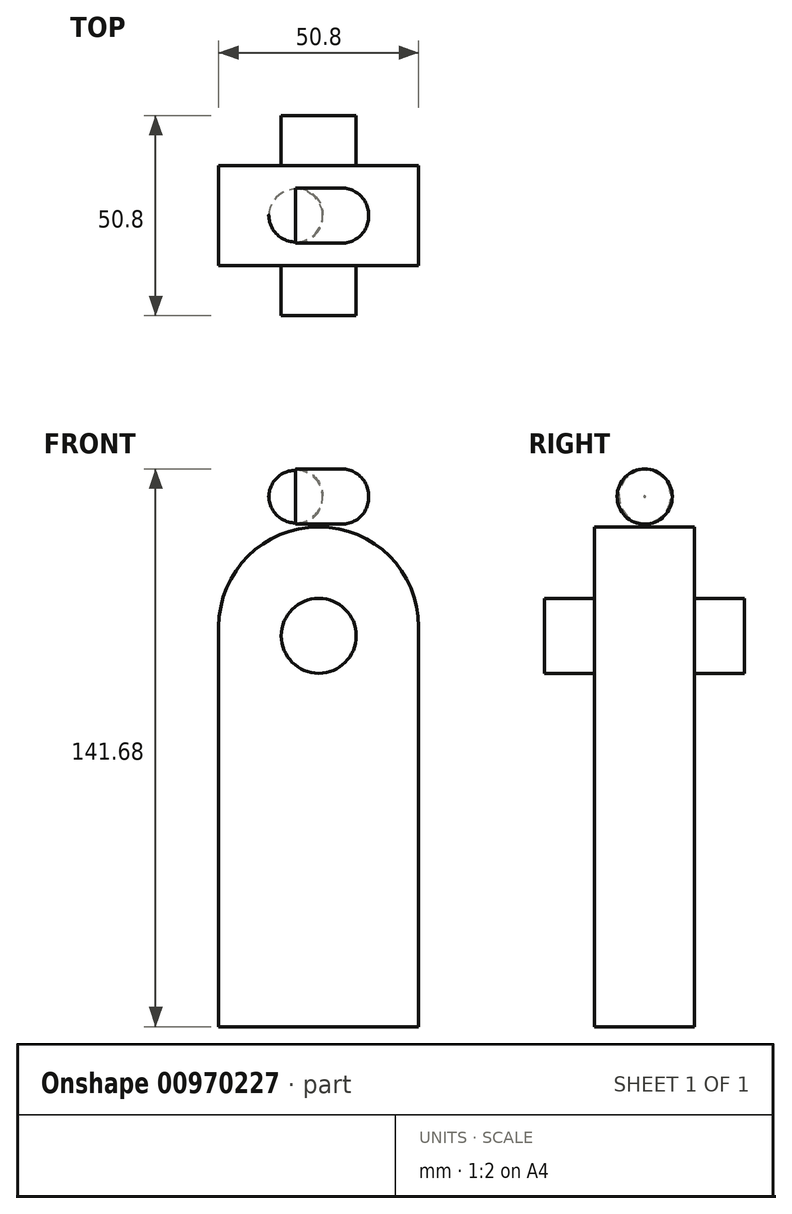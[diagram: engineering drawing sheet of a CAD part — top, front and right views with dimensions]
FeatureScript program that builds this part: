
annotation { "Feature Type Name" : "Feature", "Feature Type Description" : "" }
export const myFeature = defineFeature(function(context is Context, id is Id, definition is map)
    precondition{}
    {
        {
            var Q0;
            Q0=qCreatedBy(makeId("Front.planeOp"),FACE);
            var sketch = newSketch(context, id + "F0", { "sketchPlane" : qUnion([Q0])});
            skLineSegment(sketch, "E0.bottom", {"start": v(25.4, -63.5) * mm, "end": v(-25.4, -63.5) * mm});
            skLineSegment(sketch, "E0.top", {"start": v(25.4, 63.5) * mm, "end": v(-25.4, 63.5) * mm});
            skLineSegment(sketch, "E0.left", {"start": v(25.4, -63.5) * mm, "end": v(25.4, 63.5) * mm});
            skLineSegment(sketch, "E0.right", {"start": v(-25.4, -63.5) * mm, "end": v(-25.4, 63.5) * mm});
            skPoint(sketch, "E0.middle", {"position": v(0, 0) * mm});
            skSolve(sketch);
        }
        {
            var Q0;
            Q0 = qSketchRegion(id + "F0", true);
            var Q1;
            Q1=makeQuery(id+"F0.imprint","IMPRINT",FACE,{"disambiguationData":[TD([[makeQuery(id+"F0.imprint","IMPRINT",EDGE,{"derivedFrom":sQuery(id+"F0.wireOp",EDGE,"E0.bottom")}),-1.0]])]});
            extrude(context, id + "F1", {"entities" : qUnion([Q0, Q1]), "endBound" : BoundingType.SYMMETRIC, "depth" : 25.4 * mm, "offsetDistance" : 25.4 * mm});
        }
        {
            var Q0;
            Q0=makeQuery(id+"F1.opExtrude","SWEPT_EDGE",EDGE,{"disambiguationData":[OSD([sQuery(id+"F0.wireOp",EDGE,"E0.top"),sQuery(id+"F0.wireOp",EDGE,"E0.right")])]});
            var Q1;
            Q1=makeQuery(id+"F1.opExtrude","SWEPT_EDGE",EDGE,{"disambiguationData":[OSD([sQuery(id+"F0.wireOp",EDGE,"E0.top"),sQuery(id+"F0.wireOp",EDGE,"E0.left")])]});
            fillet(context, id + "F2", {"entities" : qUnion([Q0, Q1]), "radius" : 25.4 * mm, "tangentPropagation" : true, "allowEdgeOverflow" : false});
        }
        {
            var Q0;
            Q0=qCreatedBy(makeId("Front.planeOp"),FACE);
            var sketch = newSketch(context, id + "F3", { "sketchPlane" : qUnion([Q0])});
            skCircle(sketch, "E1", {"center": v(0, 35.8) * mm, "radius": 9.53 * mm});
            skSolve(sketch);
        }
        {
            var Q0;
            Q0 = qSketchRegion(id + "F3", true);
            extrude(context, id + "F4", {"entities" : qUnion([Q0]), "operationType" : NewBodyOperationType.ADD, "endBound" : BoundingType.SYMMETRIC, "depth" : 50.8 * mm, "offsetDistance" : 25.4 * mm});
        }
        {
            var Q0;
            Q0=qCreatedBy(makeId("Right.planeOp"),FACE);
            var sketch = newSketch(context, id + "F5", { "sketchPlane" : qUnion([Q0])});
            skCircle(sketch, "E2", {"center": v(0, 71.17) * mm, "radius": 7.01 * mm});
            skLineSegment(sketch, "E3", {"start": v(12.9, 64.16) * mm, "end": v(-12.9, 64.16) * mm});
            skSolve(sketch);
        }
        {
            var Q0;
            Q0 = qSketchRegion(id + "F5", true);
            extrude(context, id + "F6", {"entities" : qUnion([Q0]), "endBound" : BoundingType.SYMMETRIC, "depth" : 25.4 * mm, "offsetDistance" : 25.4 * mm});
        }
        {
            var Q0;
            Q0=makeQuery(id+"F6.opExtrude","CAP_EDGE",EDGE,{"disambiguationData":[OSD([sQuery(id+"F5.wireOp",EDGE,"E2")])],"isStart":true});
            var Q1;
            Q1=makeQuery(id+"F6.opExtrude","CAP_FACE",FACE,{"disambiguationData":[OSD([sQuery(id+"F5.wireOp",EDGE,"E2")])],"isStart":false});
            fillet(context, id + "F7", {"entities" : qUnion([Q0, Q1]), "radius" : 6.86 * mm, "tangentPropagation" : true, "allowEdgeOverflow" : false});
        }
    });
